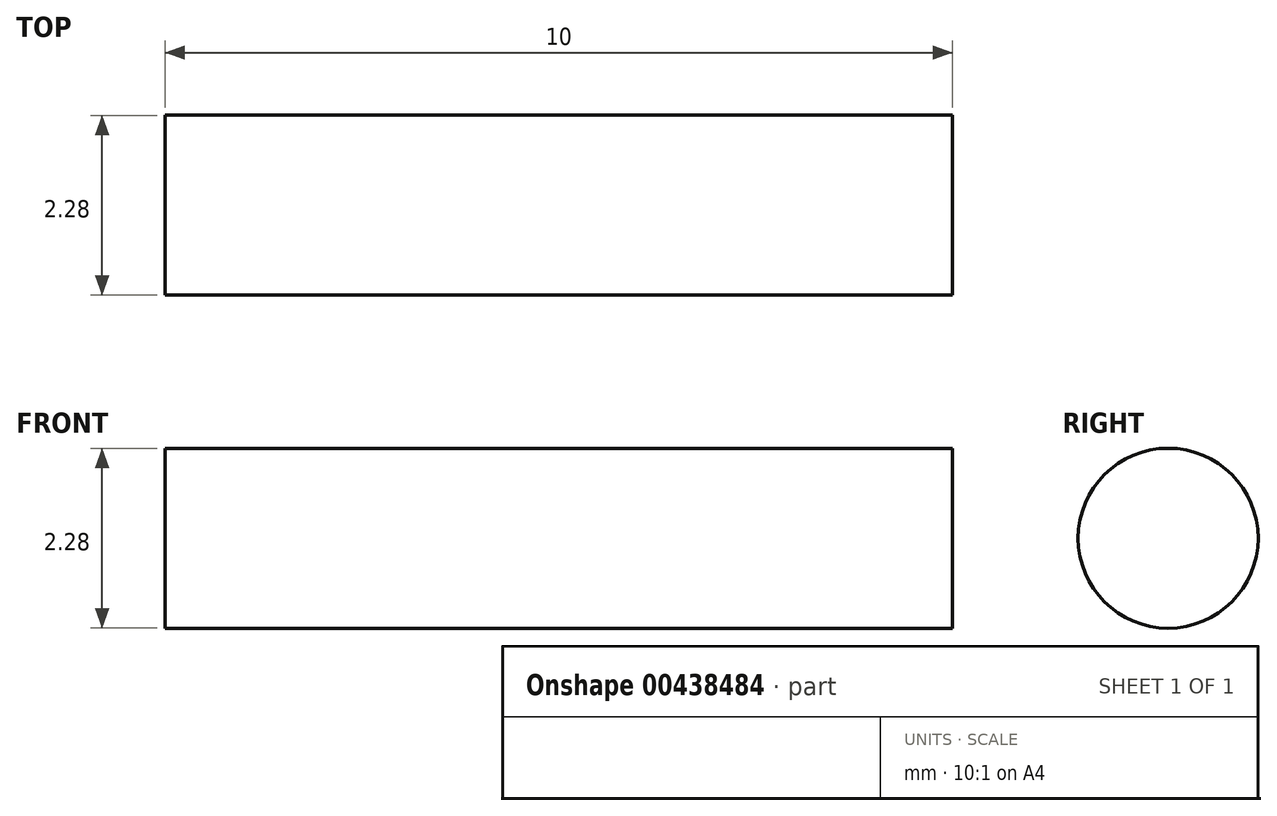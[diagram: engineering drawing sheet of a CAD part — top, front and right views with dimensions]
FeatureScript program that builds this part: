
annotation { "Feature Type Name" : "Feature", "Feature Type Description" : "" }
export const myFeature = defineFeature(function(context is Context, id is Id, definition is map)
    precondition{}
    {
        {
            var Q0;
            Q0=qCreatedBy(makeId("Top.planeOp"),FACE);
            var sketch = newSketch(context, id + "F0", { "sketchPlane" : qUnion([Q0])});
            skLineSegment(sketch, "E0.bottom", {"start": v(-6.61, -4.53) * mm, "end": v(3.39, -4.53) * mm});
            skLineSegment(sketch, "E0.top", {"start": v(-6.61, -9.6) * mm, "end": v(3.39, -9.6) * mm});
            skLineSegment(sketch, "E0.left", {"start": v(-6.61, -4.53) * mm, "end": v(-6.61, -9.6) * mm});
            skLineSegment(sketch, "E0.right", {"start": v(3.39, -4.53) * mm, "end": v(3.39, -9.6) * mm});
            skSolve(sketch);
        }
        {
            var Q0;
            Q0 = qSketchRegion(id + "F0", true);
            extrude(context, id + "F1", {"entities" : qUnion([Q0]), "depth" : 12.7 * mm});
        }
        {
            var Q0;
            Q0=makeQuery(id+"F1.opExtrude","SWEPT_FACE",FACE,{"disambiguationData":[OSD([sQuery(id+"F0.wireOp",EDGE,"E0.right")])]});
            var sketch = newSketch(context, id + "F2", { "sketchPlane" : qUnion([Q0])});
            skCircle(sketch, "E1", {"center": v(-7.36, 5.5) * mm, "radius": 1.14 * mm});
            skLineSegment(sketch, "E2.bottom", {"start": v(-10.1, 13.44) * mm, "end": v(-3.64, 13.44) * mm});
            skLineSegment(sketch, "E2.top", {"start": v(-10.1, -1) * mm, "end": v(-3.64, -1) * mm});
            skLineSegment(sketch, "E2.left", {"start": v(-10.1, 13.44) * mm, "end": v(-10.1, -1) * mm});
            skLineSegment(sketch, "E2.right", {"start": v(-3.64, 13.44) * mm, "end": v(-3.64, -1) * mm});
            skSolve(sketch);
        }
        {
            var Q0;
            Q0 = qSketchRegion(id + "F2", true);
            extrude(context, id + "F3", {"entities" : qUnion([Q0]), "operationType" : NewBodyOperationType.REMOVE, "endBound" : BoundingType.THROUGH_ALL, "oppositeDirection" : true, "depth" : 25.4 * mm});
        }
    });
